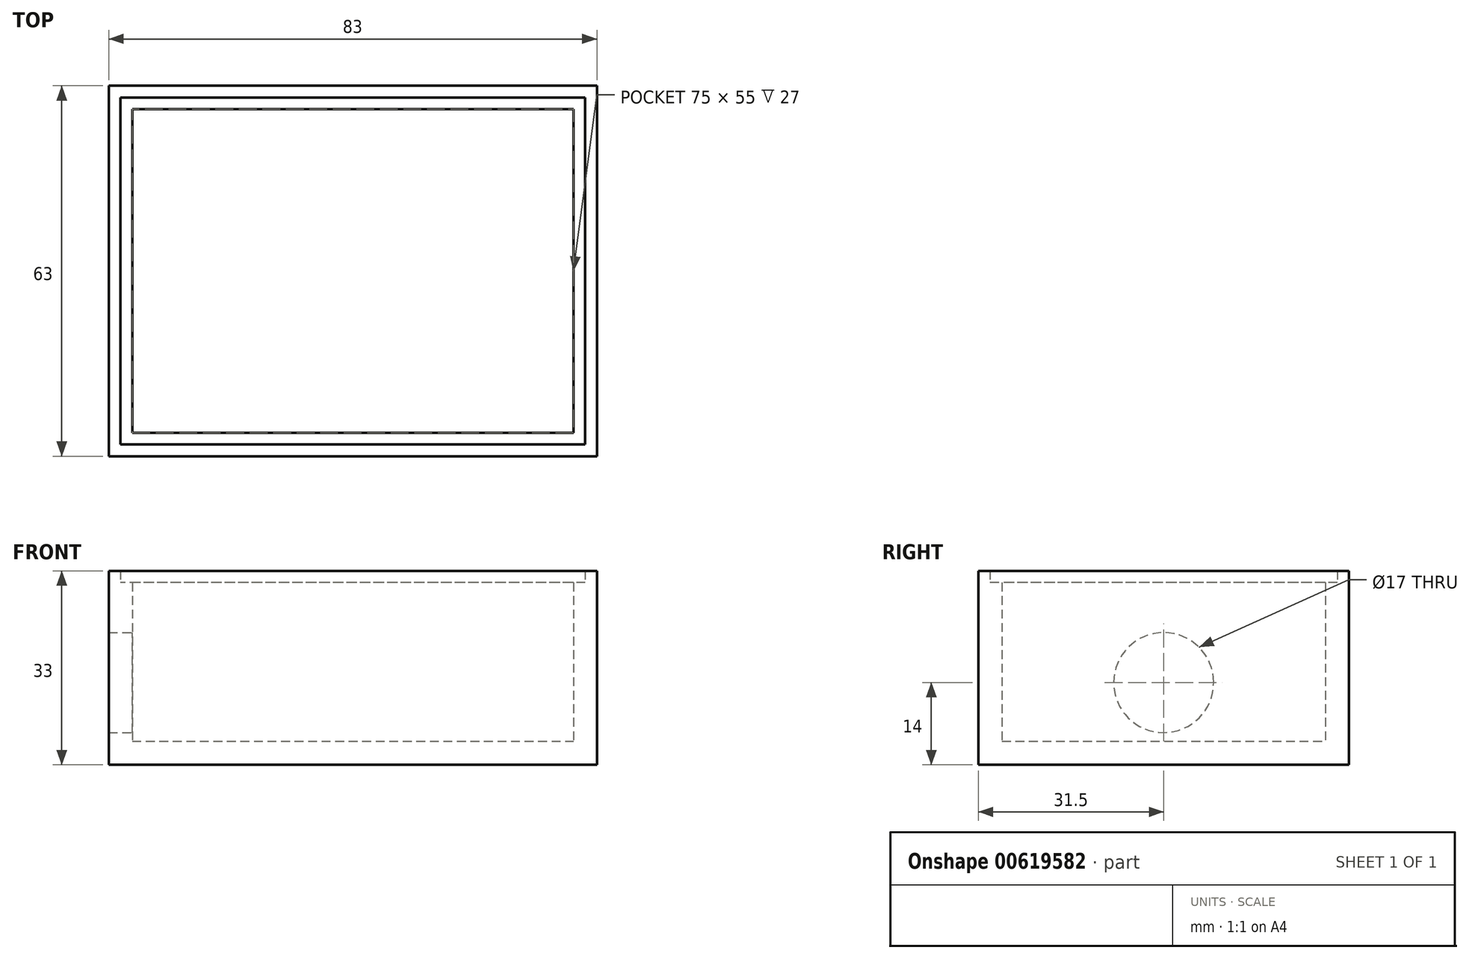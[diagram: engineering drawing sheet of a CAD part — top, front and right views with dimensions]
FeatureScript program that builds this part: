
annotation { "Feature Type Name" : "Feature", "Feature Type Description" : "" }
export const myFeature = defineFeature(function(context is Context, id is Id, definition is map)
    precondition{}
    {
        {
            var Q0;
            Q0=qCreatedBy(makeId("Top.planeOp"),FACE);
            var sketch = newSketch(context, id + "F0", { "sketchPlane" : qUnion([Q0])});
            skLineSegment(sketch, "E0.bottom", {"start": v(37.5, 27.5) * mm, "end": v(-37.5, 27.5) * mm});
            skLineSegment(sketch, "E0.top", {"start": v(37.5, -27.5) * mm, "end": v(-37.5, -27.5) * mm});
            skLineSegment(sketch, "E0.left", {"start": v(37.5, 27.5) * mm, "end": v(37.5, -27.5) * mm});
            skLineSegment(sketch, "E0.right", {"start": v(-37.5, 27.5) * mm, "end": v(-37.5, -27.5) * mm});
            skPoint(sketch, "E0.middle", {"position": v(0, 0) * mm});
            skLineSegment(sketch, "E1.0", {"start": v(41.5, 31.5) * mm, "end": v(-41.5, 31.5) * mm});
            skLineSegment(sketch, "E1.1", {"start": v(41.5, 31.5) * mm, "end": v(41.5, -31.5) * mm});
            skLineSegment(sketch, "E1.2", {"start": v(41.5, -31.5) * mm, "end": v(-41.5, -31.5) * mm});
            skLineSegment(sketch, "E1.3", {"start": v(-41.5, 31.5) * mm, "end": v(-41.5, -31.5) * mm});
            skLineSegment(sketch, "E2.0", {"start": v(39.5, 29.5) * mm, "end": v(-39.5, 29.5) * mm});
            skLineSegment(sketch, "E2.1", {"start": v(39.5, 29.5) * mm, "end": v(39.5, -29.5) * mm});
            skLineSegment(sketch, "E2.2", {"start": v(39.5, -29.5) * mm, "end": v(-39.5, -29.5) * mm});
            skLineSegment(sketch, "E2.3", {"start": v(-39.5, 29.5) * mm, "end": v(-39.5, -29.5) * mm});
            skArc(sketch, "E3", {"start": v(-7.5, 31.5) * mm, "mid": v(0, 39) * mm, "end": v(7.5, 31.5) * mm});
            skArc(sketch, "E4", {"start": v(7.5, -31.5) * mm, "mid": v(0, -39) * mm, "end": v(-7.5, -31.5) * mm});
            skPoint(sketch, "E4.startSnap0", {"position": v(0, -31.5) * mm});
            skArc(sketch, "E5", {"start": v(3.5, -31.5) * mm, "mid": v(0, -35) * mm, "end": v(-3.5, -31.5) * mm});
            skArc(sketch, "E6", {"start": v(-3.5, 31.5) * mm, "mid": v(0, 35) * mm, "end": v(3.5, 31.5) * mm});
            skSolve(sketch);
        }
        {
            var Q0;
            Q0=makeQuery(id+"F0.imprint","IMPRINT",FACE,{"disambiguationData":[TD([[makeQuery(id+"F0.imprint","IMPRINT",EDGE,{"derivedFrom":sQuery(id+"F0.wireOp",EDGE,"E0.bottom")}),1.0]])]});
            var Q1;
            Q1=makeQuery(id+"F0.imprint","IMPRINT",FACE,{"disambiguationData":[TD([[makeQuery(id+"F0.imprint","IMPRINT",EDGE,{"derivedFrom":sQuery(id+"F0.wireOp",EDGE,"E0.left")}),1.0]])]});
            var Q2;
            {var subQ3=sQuery(id+"F0.wireOp",EDGE,"E0.bottom");Q2=makeQuery(id+"F0.imprint","IMPRINT",FACE,{"disambiguationData":[TD([[makeQuery(id+"F0.imprint","IMPRINT",EDGE,{"derivedFrom":subQ3}),-1.0]])]});}
            var Q3;
            {var subQ0=sQuery(id+"F0.wireOp",EDGE,"E4");Q3=makeQuery(id+"F0.imprint","IMPRINT",FACE,{"disambiguationData":[TD([[makeQuery(id+"F0.imprint","IMPRINT",EDGE,{"derivedFrom":subQ0}),-1.0]])]});}
            var Q4;
            {var subQ0=sQuery(id+"F0.wireOp",EDGE,"E3");Q4=makeQuery(id+"F0.imprint","IMPRINT",FACE,{"disambiguationData":[TD([[makeQuery(id+"F0.imprint","IMPRINT",EDGE,{"derivedFrom":subQ0}),-1.0]])]});}
            var Q5;
            {var subQ7=sQuery(id+"F0.wireOp",EDGE,"E1.1");Q5=makeQuery(id+"F0.imprint","IMPRINT",FACE,{"disambiguationData":[TD([[makeQuery(id+"F0.imprint","IMPRINT",EDGE,{"derivedFrom":subQ7}),-1.0]])]});}
            extrude(context, id + "F1", {"entities" : qUnion([Q0, Q1, Q2, Q3, Q4, Q5]), "depth" : 4 * mm, "offsetDistance" : 25 * mm});
        }
        {
            var Q0;
            Q0=makeQuery(id+"F0.imprint","IMPRINT",FACE,{"disambiguationData":[TD([[makeQuery(id+"F0.imprint","IMPRINT",EDGE,{"derivedFrom":sQuery(id+"F0.wireOp",EDGE,"E0.bottom")}),-1.0]])]});
            var Q1;
            {var subQ0=sQuery(id+"F0.wireOp",EDGE,"E0.left");Q1=makeQuery(id+"F0.imprint","IMPRINT",FACE,{"disambiguationData":[TD([[makeQuery(id+"F0.imprint","IMPRINT",EDGE,{"derivedFrom":subQ0}),1.0]])]});}
            extrude(context, id + "F2", {"entities" : qUnion([Q0, Q1]), "operationType" : NewBodyOperationType.ADD, "depth" : 31 * mm, "offsetDistance" : 25 * mm});
        }
        {
            var Q0;
            {var subQ2=sQuery(id+"F0.wireOp",EDGE,"E1.0");Q0=makeQuery(id+"F0.imprint","IMPRINT",FACE,{"disambiguationData":[TD([[makeQuery(id+"F0.imprint","IMPRINT",EDGE,{"derivedFrom":subQ2}),1.0]])]});}
            var Q1;
            {var subQ3=sQuery(id+"F0.wireOp",EDGE,"BpwxXJsW-Y4wv-4bH7-8sEr-TF1qFDjkGtqp");Q1=makeQuery(id+"F0.imprint","IMPRINT",FACE,{"disambiguationData":[TD([[makeQuery(id+"F0.imprint","IMPRINT",EDGE,{"derivedFrom":subQ3}),1.0]])]});}
            var Q2;
            {var subQ0=sQuery(id+"F0.wireOp",EDGE,"b7bS5r4u-mkCO-uhQs-6y8N-nC0bHDf0bAsM");var subQ1=sQuery(id+"F0.wireOp",EDGE,"E1.1");var subQ2=makeQuery(id+"F0.imprint","INTERSECT",VERTEX,{"derivedFrom":[subQ1,subQ0]});Q2=makeQuery(id+"F0.imprint","IMPRINT",FACE,{"disambiguationData":[TD([[makeQuery(id+"F0.imprint","IMPRINT",EDGE,{"disambiguationData":[TD([[subQ2,-1.0]])],"derivedFrom":subQ1}),-1.0]])]});}
            var Q3;
            {var subQ3=sQuery(id+"F0.wireOp",EDGE,"JAcU3vDu-t6HP-g1O3-so5M-XiaFXz2mrILz");Q3=makeQuery(id+"F0.imprint","IMPRINT",FACE,{"disambiguationData":[TD([[makeQuery(id+"F0.imprint","IMPRINT",EDGE,{"derivedFrom":subQ3}),-1.0]])]});}
            extrude(context, id + "F3", {"entities" : qUnion([Q0, Q1, Q2, Q3]), "operationType" : NewBodyOperationType.ADD, "depth" : 33 * mm, "offsetDistance" : 25 * mm});
        }
        {
            var Q0;
            Q0=qCreatedBy(makeId("Right.planeOp"),FACE);
            var sketch = newSketch(context, id + "F4", { "sketchPlane" : qUnion([Q0])});
            skLineSegment(sketch, "E7", {"start": v(0, 0) * mm, "end": v(0, 14) * mm, "construction": true});
            skLineSegment(sketch, "E8", {"start": v(0, 0) * mm, "end": v(-30.5, 0) * mm, "construction": true});
            skCircle(sketch, "E9", {"center": v(0, 14) * mm, "radius": 8.5 * mm});
            skSolve(sketch);
        }
        {
            var Q0;
            Q0=makeQuery(id+"F4.imprint","IMPRINT",FACE,{"disambiguationData":[TD([[makeQuery(id+"F4.imprint","IMPRINT",EDGE,{"derivedFrom":sQuery(id+"F4.wireOp",EDGE,"E9")}),1.0]])]});
            extrude(context, id + "F5", {"entities" : qUnion([Q0]), "operationType" : NewBodyOperationType.REMOVE, "endBound" : BoundingType.THROUGH_ALL, "oppositeDirection" : true, "depth" : 25 * mm, "offsetDistance" : 25 * mm});
        }
    });
